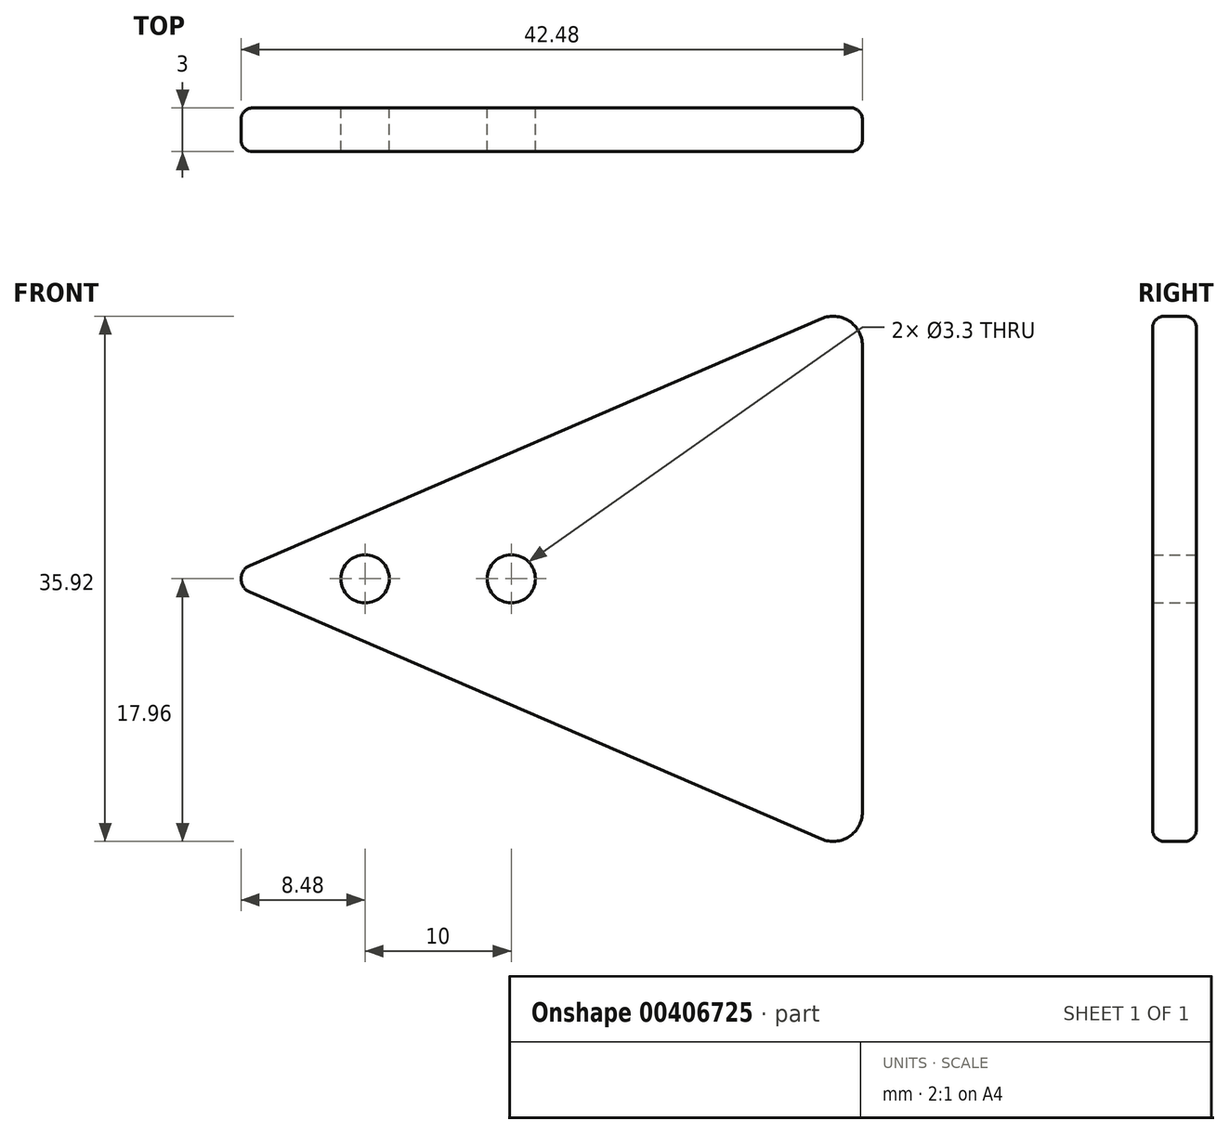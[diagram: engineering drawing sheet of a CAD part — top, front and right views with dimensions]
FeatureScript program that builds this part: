
annotation { "Feature Type Name" : "Feature", "Feature Type Description" : "" }
export const myFeature = defineFeature(function(context is Context, id is Id, definition is map)
    precondition{}
    {
        {
            var Q0;
            Q0=qCreatedBy(makeId("Front.planeOp"),FACE);
            var sketch = newSketch(context, id + "F0", { "sketchPlane" : qUnion([Q0])});
            skLineSegment(sketch, "E0", {"start": v(2.13, 0.92) * mm, "end": v(41.2, 17.8) * mm});
            skLineSegment(sketch, "E1", {"start": v(44, 15.96) * mm, "end": v(44, -15.96) * mm});
            skLineSegment(sketch, "E2", {"start": v(41.2, -17.8) * mm, "end": v(2.13, -0.92) * mm});
            skCircle(sketch, "E3", {"center": v(10, 0) * mm, "radius": 1.65 * mm});
            skCircle(sketch, "E4", {"center": v(20, 0) * mm, "radius": 1.65 * mm});
            skPoint(sketch, "E5.visualSharp", {"position": v(44, 19) * mm});
            skArc(sketch, "E5.filletArc", {"start": v(44, 15.96) * mm, "mid": v(43.1, 17.63) * mm, "end": v(41.2, 17.8) * mm});
            skPoint(sketch, "E6.visualSharp", {"position": v(44, -19) * mm});
            skArc(sketch, "E6.filletArc", {"start": v(41.2, -17.8) * mm, "mid": v(43.1, -17.63) * mm, "end": v(44, -15.96) * mm});
            skPoint(sketch, "E7.visualSharp", {"position": v(0, 0) * mm});
            skArc(sketch, "E7.filletArc", {"start": v(2.13, 0.92) * mm, "mid": v(1.52, 0) * mm, "end": v(2.13, -0.92) * mm});
            skLineSegment(sketch, "E8", {"start": v(0, 18.4) * mm, "end": v(0, -38.34) * mm});
            skArc(sketch, "E9.MirrorCS", {"start": v(-2.13, 0.92) * mm, "mid": v(-1.52, 0) * mm, "end": v(-2.13, -0.92) * mm});
            skArc(sketch, "E10.MirrorCS", {"start": v(-44, 15.96) * mm, "mid": v(-43.1, 17.63) * mm, "end": v(-41.2, 17.8) * mm});
            skArc(sketch, "E11.MirrorCS", {"start": v(-41.2, -17.8) * mm, "mid": v(-43.1, -17.63) * mm, "end": v(-44, -15.96) * mm});
            skLineSegment(sketch, "E12.MirrorCS", {"start": v(-44, 15.96) * mm, "end": v(-44, -15.96) * mm});
            skLineSegment(sketch, "E13.MirrorCS", {"start": v(-2.13, 0.92) * mm, "end": v(-41.2, 17.8) * mm});
            skLineSegment(sketch, "E14.MirrorCS", {"start": v(-41.2, -17.8) * mm, "end": v(-2.13, -0.92) * mm});
            skCircle(sketch, "E15.MirrorC", {"center": v(-10, 0) * mm, "radius": 1.65 * mm});
            skPoint(sketch, "E16.MirrorP", {"position": v(-44, -19) * mm});
            skCircle(sketch, "E17.MirrorC", {"center": v(-20, 0) * mm, "radius": 1.65 * mm});
            skPoint(sketch, "E18.MirrorP", {"position": v(-44, 19) * mm});
            skSolve(sketch);
        }
        {
            var Q0;
            Q0=makeQuery(id+"F0.imprint","IMPRINT",FACE,{"disambiguationData":[TD([[makeQuery(id+"F0.imprint","IMPRINT",EDGE,{"derivedFrom":sQuery(id+"F0.wireOp",EDGE,"E9.MirrorCS")}),-1.0]])]});
            var Q1;
            Q1=makeQuery(id+"F0.imprint","IMPRINT",FACE,{"disambiguationData":[TD([[makeQuery(id+"F0.imprint","IMPRINT",EDGE,{"derivedFrom":sQuery(id+"F0.wireOp",EDGE,"E0")}),-1.0]])]});
            extrude(context, id + "F1", {"entities" : qUnion([Q0, Q1]), "depth" : 3 * mm});
        }
        {
            var Q0;
            Q0=makeQuery(id+"F1.opExtrude","CAP_EDGE",EDGE,{"disambiguationData":[OSD([sQuery(id+"F0.wireOp",EDGE,"E12.MirrorCS")])],"isStart":false});
            var Q1;
            Q1=makeQuery(id+"F1.opExtrude","CAP_EDGE",EDGE,{"disambiguationData":[OSD([sQuery(id+"F0.wireOp",EDGE,"E13.MirrorCS")])],"isStart":true});
            var Q2;
            Q2=makeQuery(id+"F1.opExtrude","CAP_EDGE",EDGE,{"disambiguationData":[OSD([sQuery(id+"F0.wireOp",EDGE,"E0")])],"isStart":true});
            var Q3;
            Q3=makeQuery(id+"F1.opExtrude","CAP_EDGE",EDGE,{"disambiguationData":[OSD([sQuery(id+"F0.wireOp",EDGE,"E0")])],"isStart":false});
            fillet(context, id + "F2", {"entities" : qUnion([Q0, Q1, Q2, Q3]), "radius" : 0.8 * mm, "tangentPropagation" : true, "allowEdgeOverflow" : false});
        }
    });
